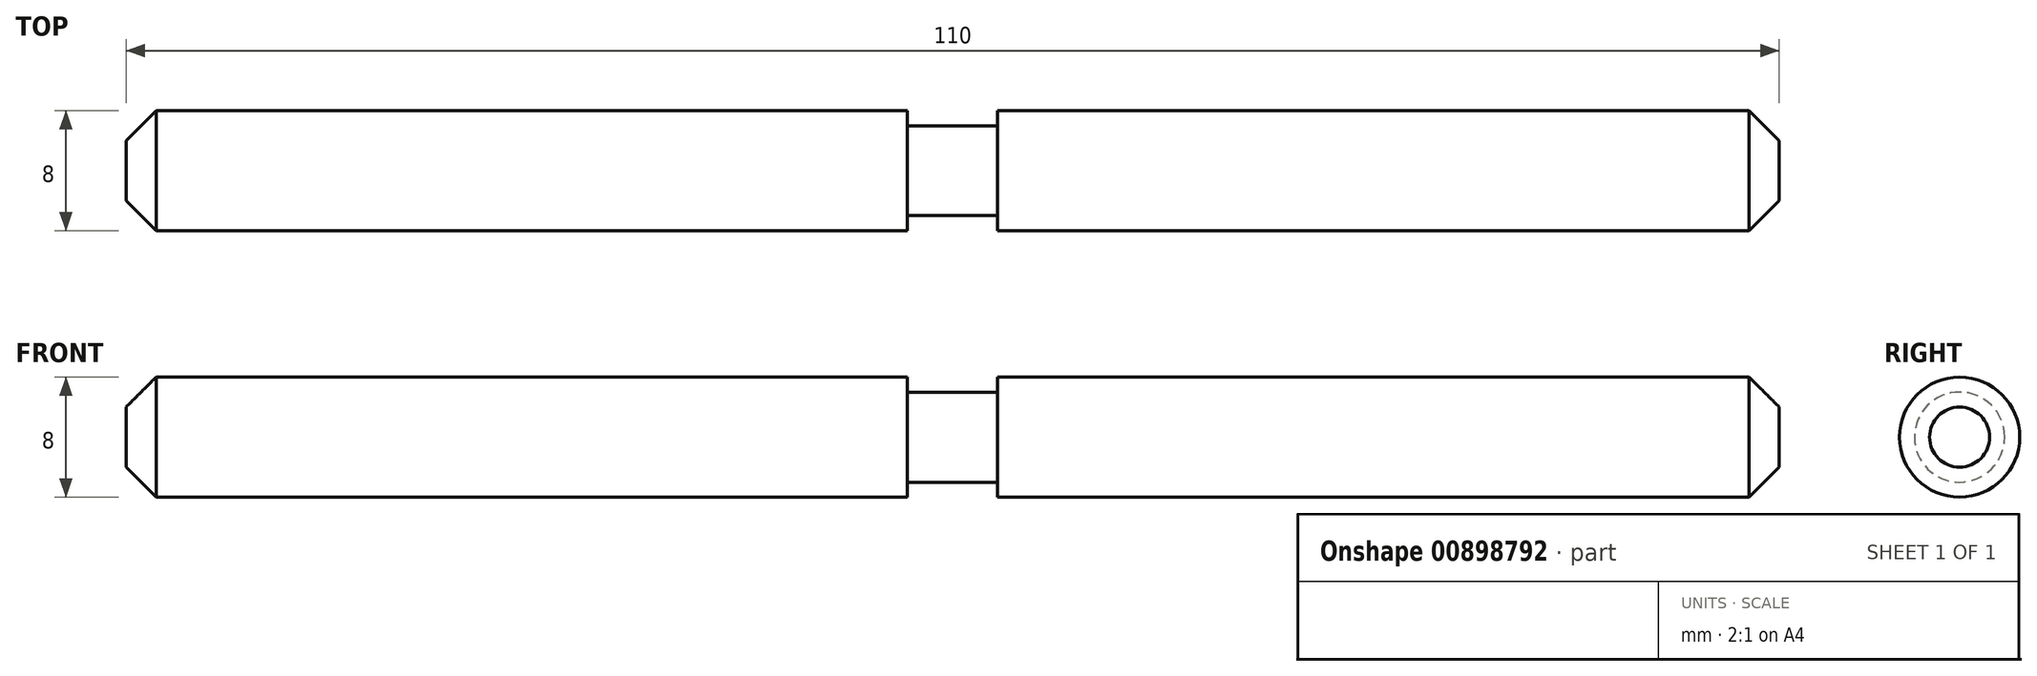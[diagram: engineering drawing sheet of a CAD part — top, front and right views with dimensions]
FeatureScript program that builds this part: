
annotation { "Feature Type Name" : "Feature", "Feature Type Description" : "" }
export const myFeature = defineFeature(function(context is Context, id is Id, definition is map)
    precondition{}
    {
        {
            var Q0;
            Q0=qCreatedBy(makeId("Top.planeOp"),FACE);
            var sketch = newSketch(context, id + "F0", { "sketchPlane" : qUnion([Q0])});
            skLineSegment(sketch, "E0.bottom", {"start": v(0, 0) * mm, "end": v(110, 0) * mm});
            skLineSegment(sketch, "E0.top", {"start": v(2, 4) * mm, "end": v(52, 4) * mm});
            skLineSegment(sketch, "E0.left", {"start": v(0, 0) * mm, "end": v(0, 2) * mm});
            skLineSegment(sketch, "E0.right", {"start": v(110, 0) * mm, "end": v(110, 2) * mm});
            skLineSegment(sketch, "E1.0", {"start": v(52, 4) * mm, "end": v(52, 3) * mm});
            skLineSegment(sketch, "E2.0", {"start": v(58, 4) * mm, "end": v(58, 3) * mm});
            skLineSegment(sketch, "E3", {"start": v(52, 3) * mm, "end": v(58, 3) * mm});
            skLineSegment(sketch, "E4.trimOffspring", {"start": v(58, 4) * mm, "end": v(108, 4) * mm});
            skLineSegment(sketch, "E5", {"start": v(0, 2) * mm, "end": v(2, 4) * mm});
            skPoint(sketch, "E6.orphan", {"position": v(0, 4) * mm});
            skLineSegment(sketch, "E7", {"start": v(110, 2) * mm, "end": v(108, 4) * mm});
            skPoint(sketch, "E8.orphan", {"position": v(110, 4) * mm});
            skSolve(sketch);
        }
        {
            var Q0;
            Q0 = qSketchRegion(id + "F0", true);
            var Q1;
            Q1=sQuery(id+"F0.wireOp",EDGE,"E0.bottom");
            revolve(context, id + "F1", {"surfaceOperationType" : NewSurfaceOperationType.NEW, "entities" : qUnion([Q0]), "axis" : qUnion([Q1]), "revolveType" : RevolveType.FULL});
        }
    });
